# Revit family: Ifö SPNK series
name_source: partatom
category: Plumbing Fixtures
revit_build: Autodesk Revit 2015 (Build: 20140606_1530(x64)
units: mm (PartAtom-declared; Revit-internal decimal feet)

## types (3) — shared parameters
Assembly Code = D2010
Brand = Ifö
Category = ShowerDoor
Color = Hardened Glass, Clear
Handle Material = Chrome
Height = 2000 mm  [stored 6.56168 ft]
Manufacturer = Geberit
ModelReference = Space
NominalHeight = 2000
Panel Length = 812 mm  [stored 2.66404 ft]
Panel Material = Hardened Glass, Clear
PanelMaterial = Hardened Glass, Clear
Profile Material = Brushed Aluminum
ProfileMaterial = Brushed aluminium
Rubber Material = Rubber
Serie = Space
Shape = Straight
Type = Building element
URL = www.ifo.dk
URL.dk = http://www.ifo.dk
URL.no = http://www.ifosanitar.no
URL.se = http://www.ifo.se
Without Lining = No
ifcExportAs = IfcFurnitureType
ifcExportType = USERDEFINED
zero-valued in all types: NominalDepth

## per-type parameters (varying)
| type | BIMObjectName | Features | Handle Visibility | Metal Lining | Model | NominalWidth | Rubber Lining | Size | Width |
| Ifö Space SPNK 900 | Ifö SBNK series | feature1, feature2, feature100 | No | Yes | 059900090 - Ifö Space SPNK 900 | 883 mm  [stored 2.89698 ft] | No | 883x2000x0 | 883 mm  [stored 2.89698 ft] |
| Ifö Space SPNK 900 knob |  | feature1, feature2, feature98 | Yes | No | 059900190- Ifö Space SPNK 900 knopp | 883 mm  [stored 2.89698 ft] | Yes | 883x2000x0 | 883 mm  [stored 2.89698 ft] |
| Ifö Space SPNK 900 H |  | feature1, feature2, feature99 | Yes | No | 059900190- Ifö Space SPNK 900 knopp | 900 mm  [stored 2.95276 ft] | Yes | 900x2000x0 | 900 mm  [stored 2.95276 ft] |

note: column(s) folded — value = type name in every type: Description, Name

note: [stored X ft] marks values corroborated as IEEE doubles in the binary element streams (Revit-internal decimal feet)

## geometry (parser evidence)
native form markers: Blend x12, Sweep x2
no freeform markers — native parametric forms only
